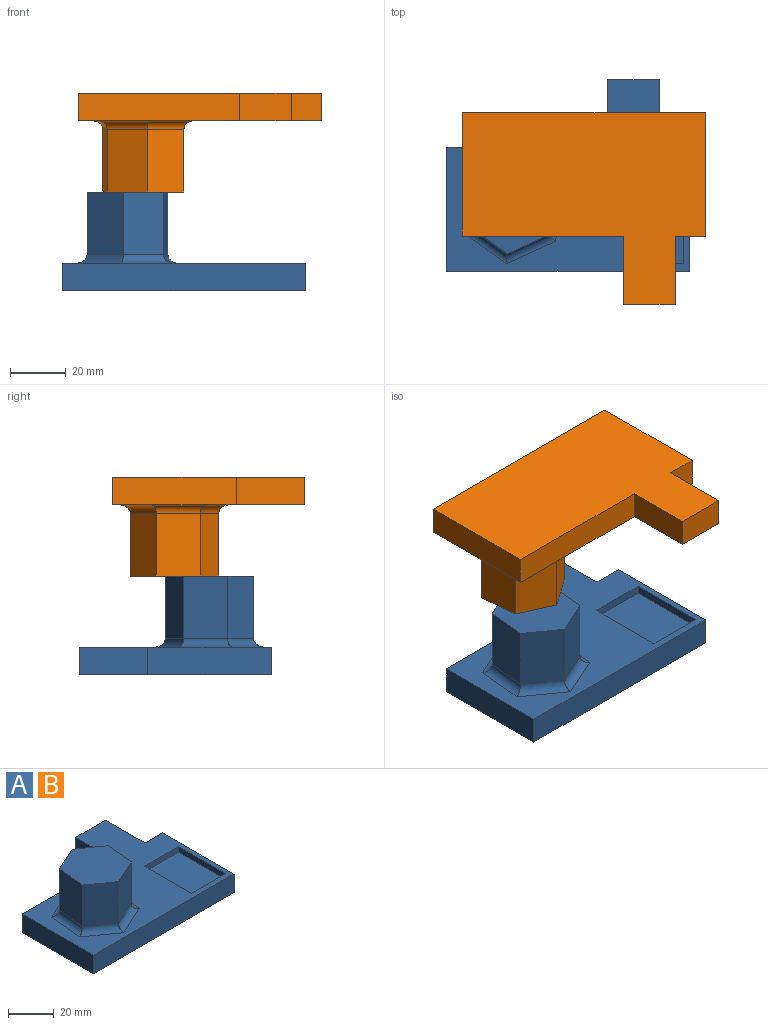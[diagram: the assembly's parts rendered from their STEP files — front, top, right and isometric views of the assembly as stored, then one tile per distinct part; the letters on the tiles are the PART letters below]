
ASSEMBLY  parts=2 mates=1
PART A: 28 faces, bbox 86.9x68.5x35.4 mm
  f0: plane 86.91x68.55mm, normal (0,0,1), area 2688.7mm2, adj f1,f2,f3,f4,f5,f6,f7,f8
  f1: plane 44.15x10mm, normal (1,0,0), area 441.5mm2, adj f0,f2,f8,f9
  f2: plane 10.84x10mm, normal (0,1,0), area 108.4mm2, adj f0,f1,f3,f9
  f3: plane 24.4x10mm, normal (1,0,0), area 244mm2, adj f0,f2,f4,f9
  f4: plane 18.4x10mm, normal (0,1,0), area 184mm2, adj f0,f3,f5,f9
  f5: plane 24.4x10mm, normal (-1,0,0), area 244mm2, adj f0,f4,f6,f9
  f6: plane 57.67x10mm, normal (0,1,0), area 576.7mm2, adj f0,f5,f7,f9
  f7: plane 44.15x10mm, normal (-1,0,0), area 441.5mm2, adj f0,f6,f8,f9
  f8: plane 86.91x10mm, normal (0,-1,0), area 869.1mm2, adj f0,f1,f7,f9
  f9: plane 86.91x68.55mm, normal (0,0,-1), area 4286.2mm2, adj f1,f2,f3,f4,f5,f6,f7,f8
  f10: plane 22.33x14.48mm, normal (-0.41,0.91,0), area 355.1mm2, adj f11,f15,f16,f18
  f11: plane 22.33x15.82mm, normal (-1,0.1,0), area 355.1mm2, adj f10,f12,f16,f17
  f12: plane 22.33x12.93mm, normal (-0.58,-0.81,0), area 355.1mm2, adj f11,f13,f16,f19
  f13: plane 22.33x14.48mm, normal (0.41,-0.91,0), area 355.1mm2, adj f12,f14,f16,f21
  f14: plane 22.33x15.82mm, normal (1,-0.1,0), area 355.1mm2, adj f13,f15,f16,f22
  f15: plane 22.33x12.93mm, normal (0.58,0.81,0), area 355.1mm2, adj f10,f14,f16,f20
  f16: plane 31.65x28.95mm, normal (0,0,1), area 656.7mm2, adj f10,f11,f12,f13,f14,f15
  f17: cylinder r=3.07mm len=19.64mm, axis (-0.1,-1,0), area 82.8mm2, adj f0,f11,f18,f19
  f18: cylinder r=3.07mm len=18.97mm, axis (-0.91,-0.41,0), area 82.8mm2, adj f0,f10,f17,f20
  f19: cylinder r=3.07mm len=17.59mm, axis (0.81,-0.58,0), area 82.8mm2, adj f0,f12,f17,f21
  f20: cylinder r=3.07mm len=17.59mm, axis (-0.81,0.58,0), area 82.8mm2, adj f0,f15,f18,f22
  f21: cylinder r=3.07mm len=18.97mm, axis (0.91,0.41,0), area 82.8mm2, adj f0,f13,f19,f22
  f22: cylinder r=3.07mm len=19.64mm, axis (0.1,1,0), area 82.8mm2, adj f0,f14,f20,f21
  f23: plane 29.14x3.05mm, normal (1,0,0), area 88.8mm2, adj f0,f24,f26,f27
  f24: plane 21.14x3.05mm, normal (0,1,0), area 64.4mm2, adj f0,f23,f25,f27
  f25: plane 29.14x3.05mm, normal (-1,0,0), area 88.8mm2, adj f0,f24,f26,f27
  f26: plane 21.14x3.05mm, normal (0,-1,0), area 64.4mm2, adj f0,f23,f25,f27
  f27: plane 29.14x21.14mm, normal (0,0,1), area 615.9mm2, adj f23,f24,f25,f26
PART B: same geometry as A
PLACE A at identity
PLACE B rot(axis=(1,0,0),180deg) t=(5.69,12.54,70.8)mm
MATE fastened B.f16 <-> A.f16  axis (0,0,-1) through (-20.22,0,35.4)mm
